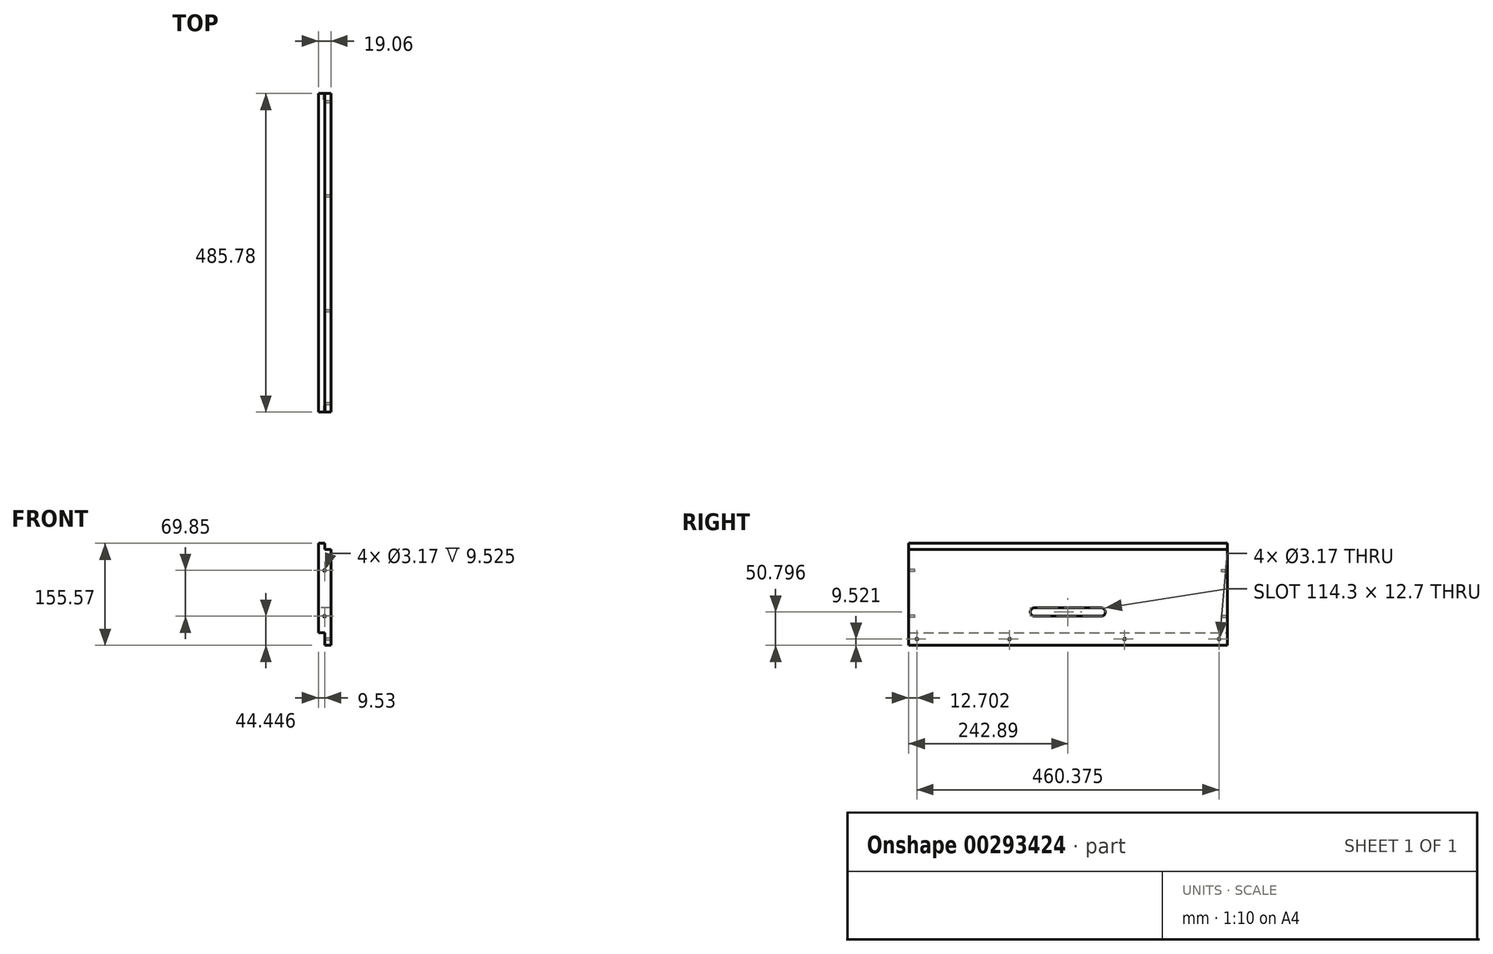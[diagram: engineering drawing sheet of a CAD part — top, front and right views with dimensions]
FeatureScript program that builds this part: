
annotation { "Feature Type Name" : "Feature", "Feature Type Description" : "" }
export const myFeature = defineFeature(function(context is Context, id is Id, definition is map)
    precondition{}
    {
        {
            var Q0;
            Q0=qCreatedBy(makeId("Right.planeOp"),FACE);
            var sketch = newSketch(context, id + "F0", { "sketchPlane" : qUnion([Q0])});
            skLineSegment(sketch, "E0.bottom", {"start": v(242.89, 216.38) * mm, "end": v(-242.89, 216.38) * mm});
            skLineSegment(sketch, "E0.top", {"start": v(242.89, -158.27) * mm, "end": v(-242.89, -158.27) * mm});
            skLineSegment(sketch, "E0.left", {"start": v(242.89, 216.38) * mm, "end": v(242.89, -158.27) * mm});
            skLineSegment(sketch, "E0.right", {"start": v(-242.89, 216.38) * mm, "end": v(-242.89, -158.27) * mm});
            skPoint(sketch, "E0.middle", {"position": v(0, 29.05) * mm});
            skLineSegment(sketch, "E1.bottom", {"start": v(-242.89, 216.38) * mm, "end": v(242.89, 216.38) * mm});
            skLineSegment(sketch, "E1.top", {"start": v(-242.89, -139.22) * mm, "end": v(242.89, -139.22) * mm});
            skLineSegment(sketch, "E1.left", {"start": v(-242.89, 216.38) * mm, "end": v(-242.89, -139.22) * mm});
            skLineSegment(sketch, "E1.right", {"start": v(242.89, 216.38) * mm, "end": v(242.89, -139.22) * mm});
            skLineSegment(sketch, "E2.bottom", {"start": v(252.41, 216.38) * mm, "end": v(-252.41, 216.38) * mm, "construction": true});
            skLineSegment(sketch, "E2.top", {"start": v(252.41, -158.27) * mm, "end": v(-252.41, -158.27) * mm, "construction": true});
            skLineSegment(sketch, "E2.left", {"start": v(252.41, 216.38) * mm, "end": v(252.41, -158.27) * mm, "construction": true});
            skLineSegment(sketch, "E2.right", {"start": v(-252.41, 216.38) * mm, "end": v(-252.41, -158.27) * mm, "construction": true});
            skLineSegment(sketch, "E3", {"start": v(-242.89, -12.22) * mm, "end": v(242.89, -12.22) * mm});
            skLineSegment(sketch, "E4", {"start": v(242.89, -2.7) * mm, "end": v(-242.89, -2.7) * mm});
            skLineSegment(sketch, "E5.bottom", {"start": v(50.8, -101.12) * mm, "end": v(-50.8, -101.12) * mm});
            skLineSegment(sketch, "E5.top", {"start": v(50.8, -113.82) * mm, "end": v(-50.8, -113.82) * mm});
            skArc(sketch, "E6", {"start": v(50.8, -113.82) * mm, "mid": v(57.15, -107.47) * mm, "end": v(50.8, -101.12) * mm});
            skArc(sketch, "E7", {"start": v(-50.8, -101.12) * mm, "mid": v(-57.15, -107.47) * mm, "end": v(-50.8, -113.82) * mm});
            skLineSegment(sketch, "E8", {"start": v(-242.89, -148.75) * mm, "end": v(242.89, -148.75) * mm, "construction": true});
            skCircle(sketch, "E9", {"center": v(-230.19, -148.75) * mm, "radius": 1.59 * mm});
            skCircle(sketch, "E10", {"center": v(230.19, -148.75) * mm, "radius": 1.59 * mm});
            skCircle(sketch, "E11", {"center": v(-88.9, -148.75) * mm, "radius": 1.59 * mm});
            skCircle(sketch, "E12", {"center": v(86.36, -148.75) * mm, "radius": 1.59 * mm});
            skSolve(sketch);
        }
        {
            var Q0;
            Q0=makeQuery(id+"F0.imprint","IMPRINT",FACE,{"disambiguationData":[TD([[makeQuery(id+"F0.imprint","IMPRINT",EDGE,{"derivedFrom":sQuery(id+"F0.wireOp",EDGE,"E0.top")}),-1.0]])]});
            var Q1;
            {var subQ2=sQuery(id+"F0.wireOp",EDGE,"E1.top");Q1=makeQuery(id+"F0.imprint","IMPRINT",FACE,{"disambiguationData":[TD([[makeQuery(id+"F0.imprint","IMPRINT",EDGE,{"derivedFrom":subQ2}),1.0]])]});}
            extrude(context, id + "F1", {"entities" : qUnion([Q0, Q1]), "depth" : 9.52 * mm});
        }
        {
            var Q0;
            {var subQ2=sQuery(id+"F0.wireOp",EDGE,"E1.top");Q0=makeQuery(id+"F0.imprint","IMPRINT",FACE,{"disambiguationData":[TD([[makeQuery(id+"F0.imprint","IMPRINT",EDGE,{"derivedFrom":subQ2}),1.0]])]});}
            var Q1;
            {var subQ0=sQuery(id+"F0.wireOp",EDGE,"E3");Q1=makeQuery(id+"F0.imprint","IMPRINT",FACE,{"disambiguationData":[TD([[makeQuery(id+"F0.imprint","IMPRINT",EDGE,{"derivedFrom":subQ0}),1.0]])]});}
            extrude(context, id + "F2", {"entities" : qUnion([Q0, Q1]), "operationType" : NewBodyOperationType.ADD, "oppositeDirection" : true, "depth" : 9.52 * mm});
        }
        {
            var Q0;
            {var subQ0=sQuery(id+"F0.wireOp",EDGE,"E1.left");Q0=makeQuery(id+"F2.boolean.opBoolean","MERGE",FACE,{"derivedFrom":[makeQuery(id+"F1.opExtrude","SWEPT_FACE",FACE,{"disambiguationData":[OSD([sQuery(id+"F0.wireOp",EDGE,"E0.right"),subQ0])]}),makeQuery(id+"F2.opExtrude","SWEPT_FACE",FACE,{"disambiguationData":[OSD([subQ0])]})]});}
            var sketch = newSketch(context, id + "F3", { "sketchPlane" : qUnion([Q0])});
            skCircle(sketch, "E13", {"center": v(0, -113.82) * mm, "radius": 1.59 * mm});
            skCircle(sketch, "E14", {"center": v(0, -43.97) * mm, "radius": 1.59 * mm});
            skSolve(sketch);
        }
        {
            var Q0;
            {var subQ0=sQuery(id+"F0.wireOp",EDGE,"E1.right");Q0=makeQuery(id+"F2.boolean.opBoolean","MERGE",FACE,{"derivedFrom":[makeQuery(id+"F1.opExtrude","SWEPT_FACE",FACE,{"disambiguationData":[OSD([sQuery(id+"F0.wireOp",EDGE,"E0.left"),subQ0])]}),makeQuery(id+"F2.opExtrude","SWEPT_FACE",FACE,{"disambiguationData":[OSD([subQ0])]})]});}
            var sketch = newSketch(context, id + "F4", { "sketchPlane" : qUnion([Q0])});
            skCircle(sketch, "E15", {"center": v(0, -113.82) * mm, "radius": 1.59 * mm});
            skCircle(sketch, "E16", {"center": v(0, -43.97) * mm, "radius": 1.59 * mm});
            skSolve(sketch);
        }
        {
            var Q0;
            Q0=makeQuery(id+"F4.imprint","IMPRINT",FACE,{"disambiguationData":[TD([[makeQuery(id+"F4.imprint","IMPRINT",EDGE,{"derivedFrom":sQuery(id+"F4.wireOp",EDGE,"E16")}),1.0]])]});
            var Q1;
            Q1=makeQuery(id+"F4.imprint","IMPRINT",FACE,{"disambiguationData":[TD([[makeQuery(id+"F4.imprint","IMPRINT",EDGE,{"derivedFrom":sQuery(id+"F4.wireOp",EDGE,"E15")}),1.0]])]});
            extrude(context, id + "F5", {"entities" : qUnion([Q0, Q1]), "operationType" : NewBodyOperationType.REMOVE, "oppositeDirection" : true, "depth" : 9.52 * mm});
        }
        {
            var Q0;
            Q0=makeQuery(id+"F3.imprint","IMPRINT",FACE,{"disambiguationData":[TD([[makeQuery(id+"F3.imprint","IMPRINT",EDGE,{"derivedFrom":sQuery(id+"F3.wireOp",EDGE,"E13")}),1.0]])]});
            var Q1;
            Q1=makeQuery(id+"F3.imprint","IMPRINT",FACE,{"disambiguationData":[TD([[makeQuery(id+"F3.imprint","IMPRINT",EDGE,{"derivedFrom":sQuery(id+"F3.wireOp",EDGE,"E14")}),1.0]])]});
            extrude(context, id + "F6", {"entities" : qUnion([Q0, Q1]), "operationType" : NewBodyOperationType.REMOVE, "oppositeDirection" : true, "depth" : 9.52 * mm});
        }
    });
